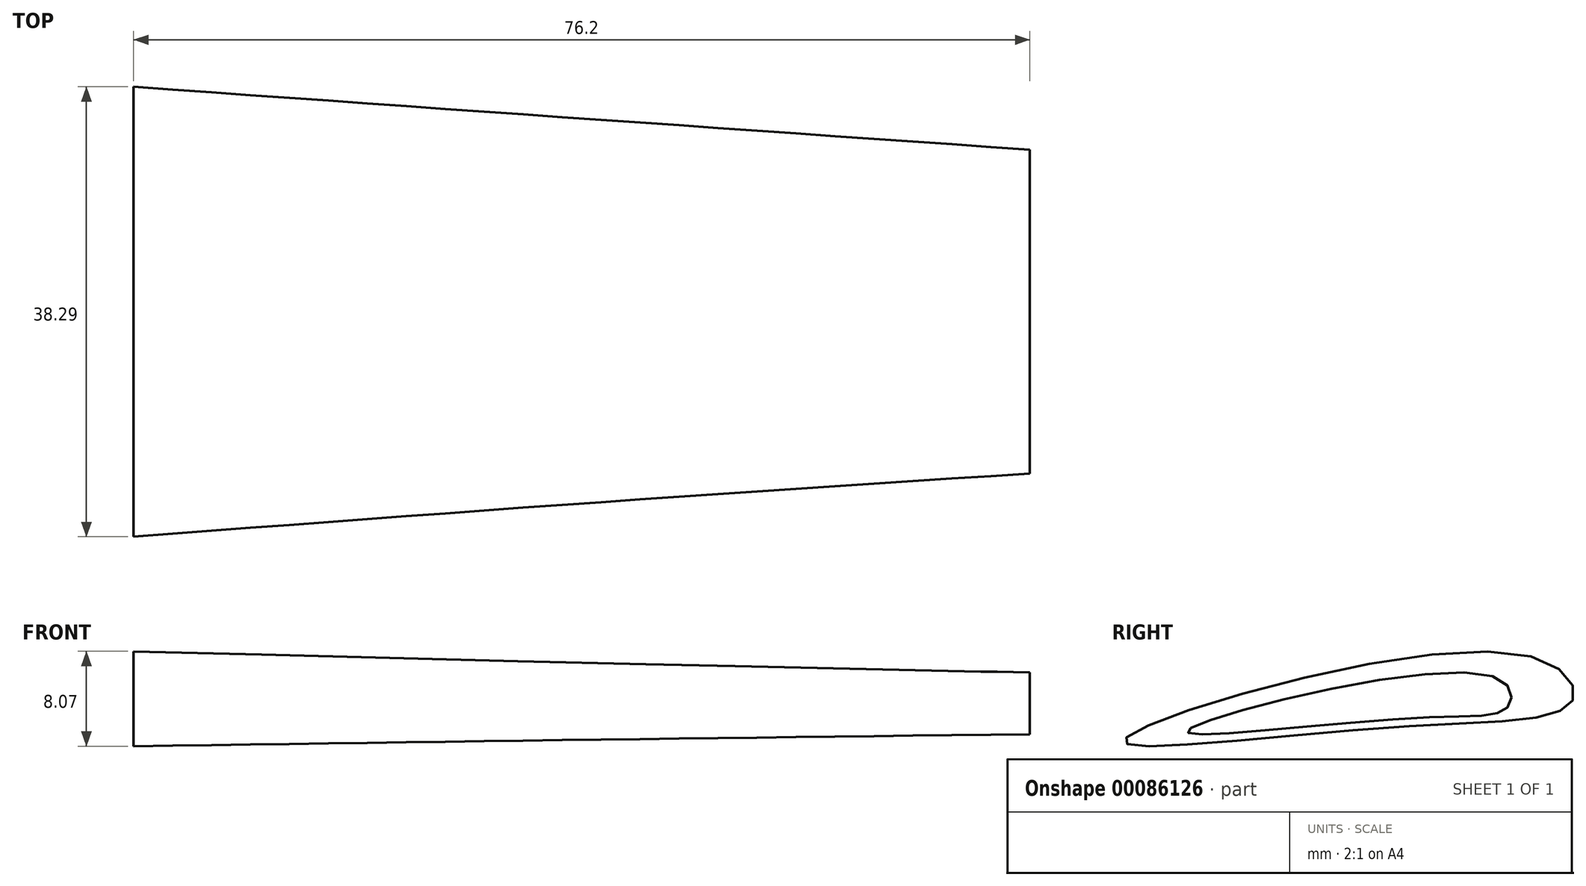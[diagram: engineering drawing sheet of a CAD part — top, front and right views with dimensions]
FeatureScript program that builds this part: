
annotation { "Feature Type Name" : "Feature", "Feature Type Description" : "" }
export const myFeature = defineFeature(function(context is Context, id is Id, definition is map)
    precondition{}
    {
        {
            var Q0;
            Q0=qCreatedBy(makeId("Right.planeOp"),FACE);
            var sketch = newSketch(context, id + "F0", { "sketchPlane" : qUnion([Q0])});
            skFitSpline(sketch, "E0", {"points": [v(-12.53, 39.98) * mm, v(-17.23, 43.96) * mm, v(-50.63, 36.66) * mm, v(-28.02, 37.69) * mm, v(-12.53, 39.98) * mm]});
            skLineSegment(sketch, "E1", {"start": v(-50.63, 36.66) * mm, "end": v(-12.53, 39.98) * mm, "construction": true});
            skSolve(sketch);
        }
        {
            var Q0;
            Q0=qCreatedBy(makeId("Right.planeOp"),FACE);
            cPlane(context, id + "F1", {"entities" : qUnion([Q0]), "cplaneType" : CPlaneType.OFFSET, "offset" : 76.2 * mm, "width" : 152.4 * mm, "height" : 152.4 * mm});
        }
        {
            var Q0;
            Q0=qCreatedBy(id+"F1.planeOp",FACE);
            var sketch = newSketch(context, id + "F2", { "sketchPlane" : qUnion([Q0])});
            skFitSpline(sketch, "E2", {"points": [v(-17.95, 39.56) * mm, v(-19.37, 42.05) * mm, v(-45.27, 37.43) * mm, v(-25.76, 38.5) * mm, v(-17.95, 39.56) * mm]});
            skSolve(sketch);
        }
        {
            var Q0;
            Q0=makeQuery(id+"F0.imprint","IMPRINT",FACE,{"disambiguationData":[TD([[makeQuery(id+"F0.imprint","IMPRINT",EDGE,{"derivedFrom":sQuery(id+"F0.wireOp",EDGE,"E0")}),1.0]])]});
            var Q1;
            Q1=makeQuery(id+"F2.imprint","IMPRINT",FACE,{"disambiguationData":[TD([[makeQuery(id+"F2.imprint","IMPRINT",EDGE,{"derivedFrom":sQuery(id+"F2.wireOp",EDGE,"E2")}),1.0]])]});
            loft(context, id + "F3", {"sheetProfilesArray" : [{ "sheetProfileEntities" : qUnion([Q0]) }, { "sheetProfileEntities" : qUnion([Q1]) }]});
        }
    });
